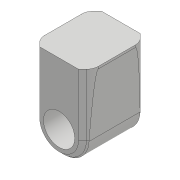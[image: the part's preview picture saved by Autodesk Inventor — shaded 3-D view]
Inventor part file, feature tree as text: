
AUTODESK INVENTOR PART (.ipt)
format: ipt  version: 2018 (Build 220112000, 112)  size: 631,296 bytes
history: native  units: mm
features: sketch x31, projected_geometry x31, extrude x28, fillet x4, hole x3, chamfer x3, mirror x1
ambient origin geometry x8: Origin, YZ Plane, XZ Plane, XY Plane, X Axis, Y Axis, Z Axis, Center Point
bodies: Solid1 (feature_tree)
feature tree (101):
  extrude  "Extrusion1"  Depth=45.0mm
  extrude  "Extrusion2"  Depth=2.25mm
  hole  "Hole1"  [1 undecoded]
  hole  "Hole2"  [1 undecoded]
  fillet  "Fillet1"  Radius=14.0mm
  extrude  "Extrusion3"  Depth=18.5mm
  extrude  "Extrusion4"  Depth=10.0mm
  extrude  "Extrusion5"  Depth=2.195mm
  extrude  "Extrusion6"  Depth=8.0mm
  hole  "Hole3"  [1 undecoded]
  extrude  "Extrusion7"  Depth=8.0mm
  extrude  "Extrusion8"  Depth=5.0mm TaperAngle=0.0deg
  extrude  "Extrusion9"  Depth=10.0mm
  extrude  "Extrusion10"  Depth=10.0mm
  extrude  "Extrusion11"  Depth=14.5mm
  extrude  "Extrusion12"  Depth=14.5mm
  extrude  "Extrusion13"  Depth=5.0mm
  extrude  "Extrusion14"  Depth=2.25mm
  extrude  "Extrusion15"  Depth=5.0mm
  extrude  "Extrusion16"  Depth=9.0mm
  extrude  "Extrusion17"  Depth=4.0mm
  chamfer  "Chamfer1"  Distance=1.0mm
  fillet  "Fillet7"  Radius=20.7mm
  fillet  "Fillet8"  Radius=32.0mm
  mirror  "Mirror1"
  extrude  "Extrusion19"  Depth=1.0mm TaperAngle=0.0deg
  extrude  "Extrusion20"  Depth=8.0mm
  extrude  "Extrusion21"  Depth=0.2mm TaperAngle=0.0deg
  extrude  "Extrusion22"  Depth=0.5mm TaperAngle=0.0deg
  extrude  "Extrusion23"  Depth=8.0mm TaperAngle=0.0deg
  chamfer  "Chamfer2"  Distance=5.0mm
  fillet  "Fillet9"  Radius=0.2mm
  extrude  "Extrusion24"  Depth=2.5mm TaperAngle=45.0deg
  extrude  "Extrusion27"  Depth=0.5mm
  extrude  "Extrusion28"  Depth=10.0mm TaperAngle=0.0deg
  extrude  "Extrusion29"  Depth=36.055mm
  chamfer  "Chamfer4"  Distance=4.2225mm
  extrude  "Extrusion30"  Depth=10.0mm
  extrude  "Extrusion31"  Depth=10.0mm TaperAngle=0.0deg
  sketch  "Sketch1"  dims[d0=24.5mm d1=45.0mm]
  sketch  "Sketch2"  dims[d2=1.95mm d3=0.0mm d4=2.25mm]
  projected_geometry  "Projected Loop1"
  sketch  "Sketch3"  dims[d5=20.0mm d6=2.25mm]
  projected_geometry  "Projected Loop2"
  sketch  "Sketch4"  dims[d7=5.25mm d8=5.25mm d9=14.0mm]
  projected_geometry  "Projected Loop3"
  sketch  "Sketch5"  dims[d10=5.25mm d11=18.5mm]
  projected_geometry  "Projected Loop4"
  sketch  "Sketch6"  dims[d12=10.0mm d13=0.0mm d14=20.5mm]
  projected_geometry  "Projected Loop5"
  sketch  "Sketch7"  dims[d15=2.0mm d16=2.195mm]
  projected_geometry  "Projected Loop6"
  sketch  "Sketch8"  dims[d17=2.0mm]
  projected_geometry  "Projected Loop7"
  sketch  "Sketch9"  dims[d18=2.4mm d19=6.0mm d20=4.4mm d21=2.0mm d22=90.0deg d23=8.0mm d24=20.594885mm d25=20.5mm]
  projected_geometry  "Projected Loop8"
  projected_geometry  "Projected Loop9"
  sketch  "Sketch10"  dims[d26=26.65mm d27=2.0mm]
  projected_geometry  "Projected Loop10"
  projected_geometry  "Projected Loop11"
  sketch  "Sketch11"  dims[d28=2.0mm]
  projected_geometry  "Projected Loop12"
  sketch  "Sketch12"  dims[d29=2.4mm d30=6.0mm d31=4.4mm d32=2.0mm d33=90.0deg d34=8.0mm d35=20.594885mm d36=0.5mm]
  sketch  "Sketch13"  dims[d37=18.0mm d38=5.0mm d39=0.0mm]
  sketch  "Sketch14"  dims[d41=10.0mm d42=0.0mm d43=24.5mm]
  projected_geometry  "Projected Loop13"
  sketch  "Sketch15"  dims[d44=1.15mm d45=0.0mm d46=10.0mm]
  sketch  "Sketch16"  dims[d47=21.0mm d48=14.5mm]
  projected_geometry  "Projected Loop14"
  sketch  "Sketch17"  dims[d49=20.0mm d50=14.5mm]
  projected_geometry  "Projected Loop15"
  sketch  "Sketch18"  dims[d51=24.5mm d52=5.0mm]
  projected_geometry  "Projected Loop16"
  sketch  "Sketch19"  dims[d53=5.0mm d54=2.25mm]
  projected_geometry  "Projected Loop17"
  sketch  "Sketch20"  dims[d55=2.25mm d56=5.0mm]
  projected_geometry  "Projected Loop18"
  sketch  "Sketch25"  dims[d57=5.0mm d58=9.0mm]
  projected_geometry  "Projected Loop22"
  sketch  "Sketch26"  dims[d59=14.75mm d60=4.0mm d61=1.0mm d62=0.0mm d63=20.7mm]
  projected_geometry  "Projected Loop23"
  sketch  "Sketch27"  dims[d64=2.4mm d65=6.0mm d66=4.4mm d67=2.0mm d68=90.0deg d69=8.0mm d70=20.594885mm d72=32.0mm]
  projected_geometry  "Projected Loop25"
  sketch  "Sketch29"  dims[d73=5.0mm d74=0.0mm d75=1.0mm d76=0.0mm]
  projected_geometry  "Projected Loop26"
  sketch  "Sketch30"  dims[d77=12.25mm d78=0.0mm d80=8.0mm]
  projected_geometry  "Projected Loop27"
  sketch  "Sketch32"  dims[d81=4.5mm d82=0.0mm d84=0.2mm d85=0.0mm]
  projected_geometry  "Projected Loop28"
  projected_geometry  "Projected Loop29"
  sketch  "Sketch36"  dims[d86=21.0mm d87=0.5mm d88=0.0mm]
  projected_geometry  "Projected Loop33"
  sketch  "Sketch37"  dims[d91=8.0mm d92=0.0mm d93=5.0mm d94=0.0mm d95=5.0mm d96=0.0mm d98=0.2mm d99=0.0mm]
  projected_geometry  "Projected Loop34"
  sketch  "Sketch41"  dims[d100=0.2mm d101=0.0mm d102=2.5mm d103=2.0mm d104=45.0deg]
  projected_geometry  "Projected Loop36"
  sketch  "Sketch44"  dims[d105=1.5mm d114=0.5mm]
  projected_geometry  "Projected Loop39"
  projected_geometry  "Projected Loop40"
  sketch  "Sketch45"  dims[d128=1.8mm d129=0.0mm d130=1.8mm d131=0.0mm d133=36.055mm d134=4.2225mm d135=4.2225mm d136=2.0mm d137=0.0mm d138=2.0mm d139=0.0mm d140=2.0mm d141=0.0mm d142=5.0mm d143=2.0mm d144=45.0deg d145=8.0mm d147=33.0mm d148=10.0mm d149=0.0mm d161=20.75mm d162=18.0mm d163=25.0mm d164=0.05mm d165=7.0mm d166=0.0mm d167=1.5mm d168=0.0mm d200=15.0mm d201=1.5mm d202=0.0mm d203=1.5mm d204=2.0mm d205=45.0deg d222=10.0mm d223=0.0mm d224=10.0mm d225=0.0mm]
  projected_geometry  "Projected Loop41"
note: 3 required parameter values undecoded (feature->parameter linkage not recoverable at this tier; creation-order binding heuristic only, values carry confidence <= 0.55)
